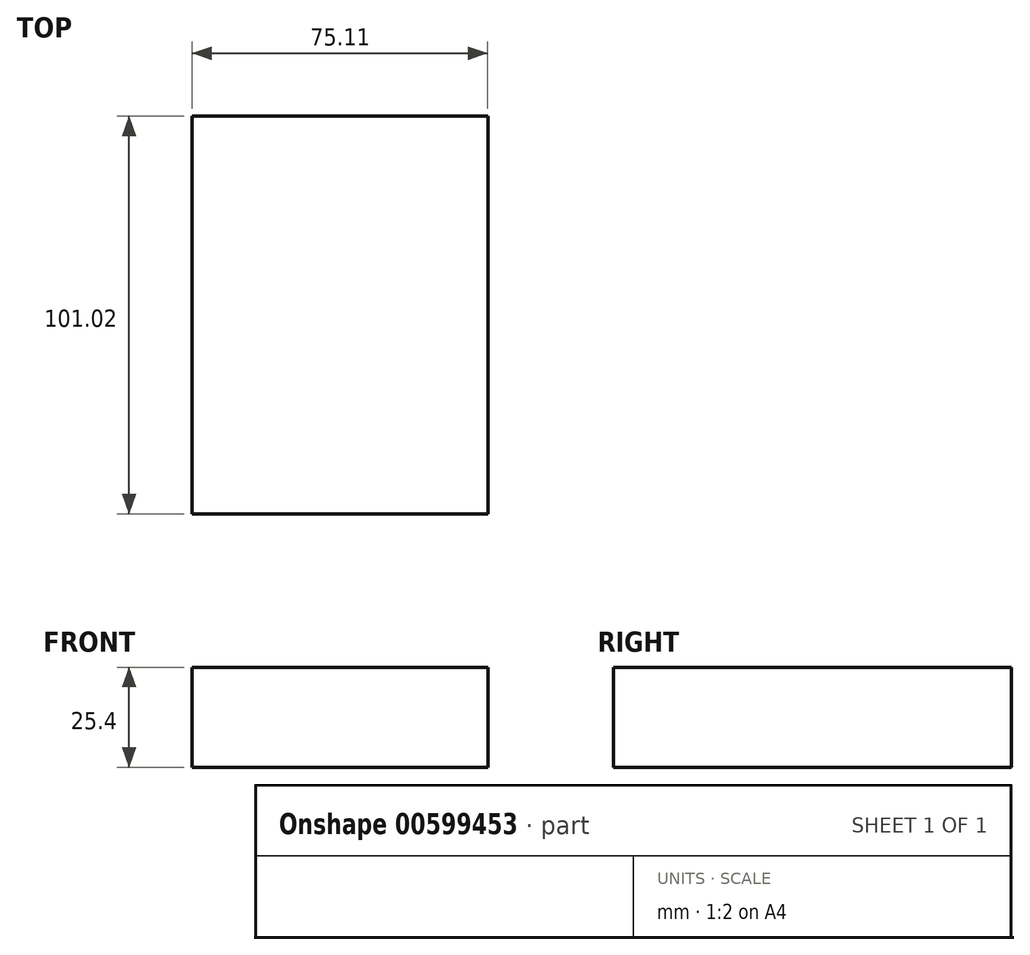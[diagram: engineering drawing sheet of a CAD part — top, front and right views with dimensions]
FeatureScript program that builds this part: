
annotation { "Feature Type Name" : "Feature", "Feature Type Description" : "" }
export const myFeature = defineFeature(function(context is Context, id is Id, definition is map)
    precondition{}
    {
        {
            var Q0;
            Q0=qCreatedBy(makeId("Top.planeOp"),FACE);
            var sketch = newSketch(context, id + "F0", { "sketchPlane" : qUnion([Q0])});
            skLineSegment(sketch, "E0.bottom", {"start": v(-44.75, 32.1) * mm, "end": v(30.36, 32.1) * mm});
            skLineSegment(sketch, "E0.top", {"start": v(-44.75, -68.93) * mm, "end": v(30.36, -68.93) * mm});
            skLineSegment(sketch, "E0.left", {"start": v(-44.75, 32.1) * mm, "end": v(-44.75, -68.93) * mm});
            skLineSegment(sketch, "E0.right", {"start": v(30.36, 32.1) * mm, "end": v(30.36, -68.93) * mm});
            skSolve(sketch);
        }
        {
            var Q0;
            Q0=makeQuery(id+"F0.imprint","IMPRINT",FACE,{"disambiguationData":[TD([[makeQuery(id+"F0.imprint","IMPRINT",EDGE,{"derivedFrom":sQuery(id+"F0.wireOp",EDGE,"E0.bottom")}),-1.0]])]});
            extrude(context, id + "F1", {"entities" : qUnion([Q0]), "depth" : 25.4 * mm, "offsetDistance" : 25.4 * mm});
        }
    });
